# Revit family: LZSTLG8WSLK
name_source: partatom
category: Plumbing Fixtures
units: mm (PartAtom-declared; Revit-internal decimal feet)

## family parameters
Always vertical = Yes
Cut with Voids When Loaded = No
OmniClass Number = 23.45.00.00
OmniClass Title = Sanitary, Laundry, and Cleaning Equipment
Part Type = Normal
Room Calculation Point = No
Round Connector Dimension = Use Diameter
Shared = No
Work Plane-Based = No

## types (1)
- LZSTLG8WSLK
    ACTIVATION BY = ELECTRONIC BOTTLE FILLER SENSOR WITH ELECTRONIC FRONT AND SIDE BUBBLER PUSHBAR
    APPROX. SHIPPING WEIGHT = 104 LBS
    BUBBLER STYLE = FLEXI-GUARD STREAMSAVER
    CHILLING OPTION = 8.0 GPH
    CW Connection = No
    DIMENSIONS = 36-3/4" X 19" X 39-1/16"
    FULL LOAD AMPS = 7
    HW Connection = No
    INSTALLATION LOCATION = INDOOR
    MOUNTING TYPE = WALL MOUNT
    NO. OF STATIONS SERVED = 2
    POWER = 115 V
    RATED WATTS = 360
    SPECIAL FEATURES = HANDS FREE, VISUAL FILTER MONITOR, FILTERED, HIGH EFFICIENCY, GREEN TICKER, LAMINAR FLOW, ANTIMICROBIAL, REAL DRAIN
    Vent Connection = No
    WASTE OUTLET = 0' - 1 1/4"
    WATER SUPPLY = 0' - 0 3/8"
    Waste Connection = No

## geometry (parser evidence)
native form markers: Blend x2, Sweep x2
no freeform markers — native parametric forms only
